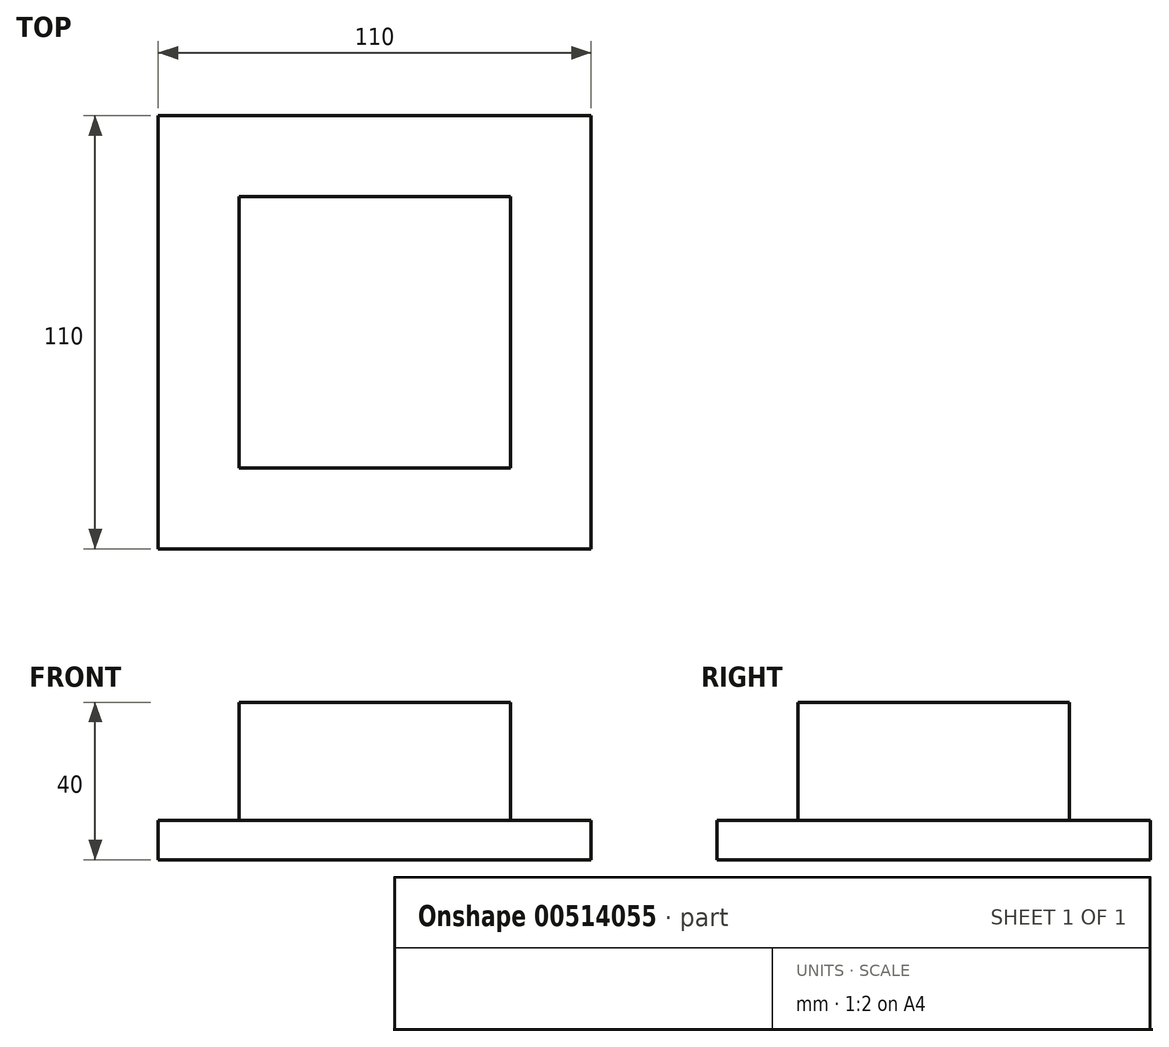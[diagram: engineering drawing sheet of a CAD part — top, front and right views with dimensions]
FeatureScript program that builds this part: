
annotation { "Feature Type Name" : "Feature", "Feature Type Description" : "" }
export const myFeature = defineFeature(function(context is Context, id is Id, definition is map)
    precondition{}
    {
        {
            var Q0;
            Q0=qCreatedBy(makeId("Top.planeOp"),FACE);
            var sketch = newSketch(context, id + "F0", { "sketchPlane" : qUnion([Q0])});
            skLineSegment(sketch, "E0.bottom", {"start": v(0, 0) * mm, "end": v(110, 0) * mm});
            skLineSegment(sketch, "E0.top", {"start": v(0, 110) * mm, "end": v(110, 110) * mm});
            skLineSegment(sketch, "E0.left", {"start": v(0, 0) * mm, "end": v(0, 110) * mm});
            skLineSegment(sketch, "E0.right", {"start": v(110, 0) * mm, "end": v(110, 110) * mm});
            skLineSegment(sketch, "E1.0", {"start": v(20.5, 89.5) * mm, "end": v(89.5, 89.5) * mm});
            skLineSegment(sketch, "E1.1", {"start": v(20.5, 20.5) * mm, "end": v(20.5, 89.5) * mm});
            skLineSegment(sketch, "E1.2", {"start": v(20.5, 20.5) * mm, "end": v(89.5, 20.5) * mm});
            skLineSegment(sketch, "E1.3", {"start": v(89.5, 20.5) * mm, "end": v(89.5, 89.5) * mm});
            skSolve(sketch);
        }
        {
            var Q0;
            Q0 = qSketchRegion(id + "F0", true);
            var Q1;
            Q1=makeQuery(id+"F0.imprint","IMPRINT",FACE,{"disambiguationData":[TD([[makeQuery(id+"F0.imprint","IMPRINT",EDGE,{"derivedFrom":sQuery(id+"F0.wireOp",EDGE,"E0.bottom")}),1.0]])]});
            extrude(context, id + "F1", {"entities" : qUnion([Q0, Q1]), "depth" : 10 * mm});
        }
        {
            var Q0;
            Q0=makeQuery(id+"F0.imprint","IMPRINT",FACE,{"disambiguationData":[TD([[makeQuery(id+"F0.imprint","IMPRINT",EDGE,{"derivedFrom":sQuery(id+"F0.wireOp",EDGE,"E1.0")}),-1.0]])]});
            extrude(context, id + "F2", {"entities" : qUnion([Q0]), "operationType" : NewBodyOperationType.ADD, "depth" : 40 * mm});
        }
    });
